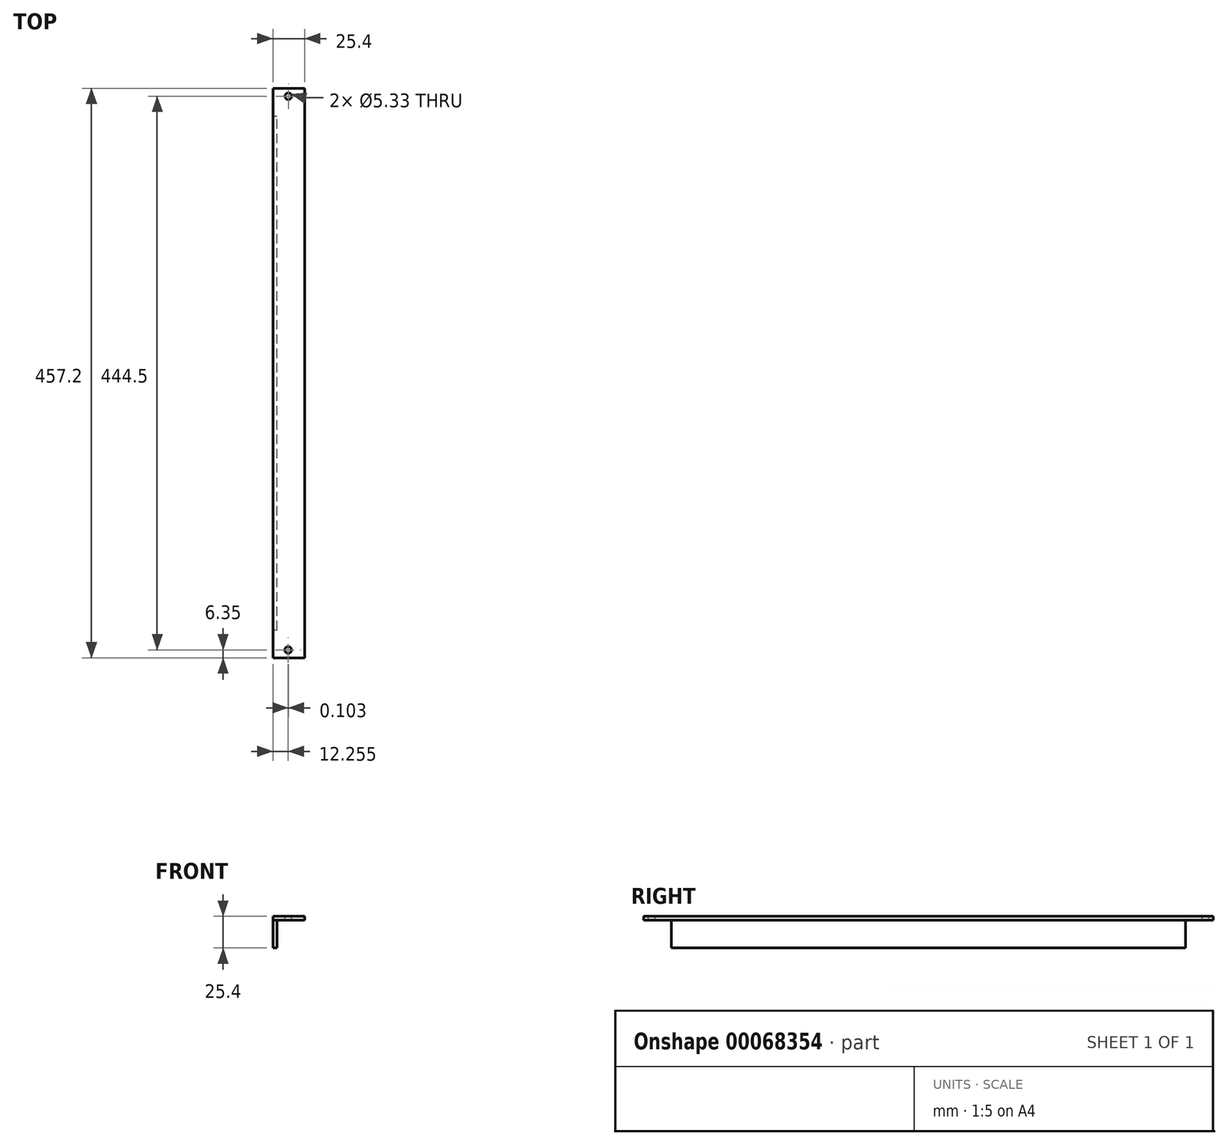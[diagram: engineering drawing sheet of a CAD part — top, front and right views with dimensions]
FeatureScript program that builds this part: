
annotation { "Feature Type Name" : "Feature", "Feature Type Description" : "" }
export const myFeature = defineFeature(function(context is Context, id is Id, definition is map)
    precondition{}
    {
        {
            var Q0;
            Q0=qCreatedBy(makeId("Front.planeOp"),FACE);
            var sketch = newSketch(context, id + "F0", { "sketchPlane" : qUnion([Q0])});
            skLineSegment(sketch, "E0.bottom", {"start": v(-1.59, 12.7) * mm, "end": v(1.59, 12.7) * mm});
            skLineSegment(sketch, "E0.top", {"start": v(-1.59, -12.7) * mm, "end": v(1.59, -12.7) * mm});
            skLineSegment(sketch, "E0.left", {"start": v(-1.59, 12.7) * mm, "end": v(-1.59, -12.7) * mm});
            skLineSegment(sketch, "E0.right", {"start": v(1.59, 9.53) * mm, "end": v(1.59, -12.7) * mm});
            skPoint(sketch, "E0.middle", {"position": v(0, 0) * mm});
            skLineSegment(sketch, "E1.bottom", {"start": v(1.59, 12.7) * mm, "end": v(23.81, 12.7) * mm});
            skLineSegment(sketch, "E1.top", {"start": v(1.59, 9.53) * mm, "end": v(23.81, 9.53) * mm});
            skLineSegment(sketch, "E1.right", {"start": v(23.81, 12.7) * mm, "end": v(23.81, 9.53) * mm});
            skSolve(sketch);
        }
        {
            var Q0;
            Q0=makeQuery(id+"F0.imprint","IMPRINT",FACE,{"disambiguationData":[TD([[makeQuery(id+"F0.imprint","IMPRINT",EDGE,{"derivedFrom":sQuery(id+"F0.wireOp",EDGE,"E0.bottom")}),-1.0]])]});
            extrude(context, id + "F1", {"entities" : qUnion([Q0]), "depth" : 457.2 * mm});
        }
        {
            var Q0;
            Q0=makeQuery(id+"F1.opExtrude","CAP_FACE",FACE,{"disambiguationData":[OSD([sQuery(id+"F0.wireOp",EDGE,"E0.bottom"),sQuery(id+"F0.wireOp",EDGE,"E0.top"),sQuery(id+"F0.wireOp",EDGE,"E0.left"),sQuery(id+"F0.wireOp",EDGE,"E0.right"),sQuery(id+"F0.wireOp",EDGE,"E1.bottom"),sQuery(id+"F0.wireOp",EDGE,"E1.top"),sQuery(id+"F0.wireOp",EDGE,"E1.right")])],"isStart":true});
            var sketch = newSketch(context, id + "F2", { "sketchPlane" : qUnion([Q0])});
            skLineSegment(sketch, "E2.bottom", {"start": v(-1.59, 9.53) * mm, "end": v(1.59, 9.53) * mm});
            skLineSegment(sketch, "E2.top", {"start": v(-1.59, -12.7) * mm, "end": v(1.59, -12.7) * mm});
            skLineSegment(sketch, "E2.left", {"start": v(-1.59, 9.53) * mm, "end": v(-1.59, -12.7) * mm});
            skLineSegment(sketch, "E2.right", {"start": v(1.59, 9.53) * mm, "end": v(1.59, -12.7) * mm});
            skSolve(sketch);
        }
        {
            var Q0;
            Q0=makeQuery(id+"F2.imprint","IMPRINT",FACE,{"disambiguationData":[TD([[makeQuery(id+"F2.imprint","IMPRINT",EDGE,{"derivedFrom":sQuery(id+"F2.wireOp",EDGE,"E2.bottom")}),-1.0]])]});
            extrude(context, id + "F3", {"entities" : qUnion([Q0]), "operationType" : NewBodyOperationType.REMOVE, "oppositeDirection" : true, "depth" : 22.22 * mm});
        }
        {
            var Q0;
            Q0=makeQuery(id+"F1.opExtrude","SWEPT_FACE",FACE,{"disambiguationData":[OSD([sQuery(id+"F0.wireOp",EDGE,"E0.left")])]});
            var sketch = newSketch(context, id + "F4", { "sketchPlane" : qUnion([Q0])});
            skLineSegment(sketch, "E3.bottom", {"start": v(457.2, -12.7) * mm, "end": v(434.98, -12.7) * mm});
            skLineSegment(sketch, "E3.top", {"start": v(457.2, 9.53) * mm, "end": v(434.98, 9.53) * mm});
            skLineSegment(sketch, "E3.left", {"start": v(457.2, -12.7) * mm, "end": v(457.2, 9.53) * mm});
            skLineSegment(sketch, "E3.right", {"start": v(434.98, -12.7) * mm, "end": v(434.98, 9.53) * mm});
            skSolve(sketch);
        }
        {
            var Q0;
            Q0=makeQuery(id+"F4.imprint","IMPRINT",FACE,{"disambiguationData":[TD([[makeQuery(id+"F4.imprint","IMPRINT",EDGE,{"derivedFrom":sQuery(id+"F4.wireOp",EDGE,"E3.bottom")}),-1.0]])]});
            extrude(context, id + "F5", {"entities" : qUnion([Q0]), "operationType" : NewBodyOperationType.REMOVE, "oppositeDirection" : true, "depth" : 3.18 * mm});
        }
        {
            var Q0;
            Q0=makeQuery(id+"F1.opExtrude","SWEPT_FACE",FACE,{"disambiguationData":[OSD([sQuery(id+"F0.wireOp",EDGE,"E0.bottom"),sQuery(id+"F0.wireOp",EDGE,"E1.bottom")])]});
            var sketch = newSketch(context, id + "F6", { "sketchPlane" : qUnion([Q0])});
            skCircle(sketch, "E4", {"center": v(10.66, -450.85) * mm, "radius": 2.67 * mm});
            skCircle(sketch, "E5", {"center": v(10.77, -6.35) * mm, "radius": 2.67 * mm});
            skSolve(sketch);
        }
        {
            var Q0;
            Q0=makeQuery(id+"F6.imprint","IMPRINT",FACE,{"disambiguationData":[TD([[makeQuery(id+"F6.imprint","IMPRINT",EDGE,{"derivedFrom":sQuery(id+"F6.wireOp",EDGE,"E4")}),1.0]])]});
            var Q1;
            Q1=makeQuery(id+"F6.imprint","IMPRINT",FACE,{"disambiguationData":[TD([[makeQuery(id+"F6.imprint","IMPRINT",EDGE,{"derivedFrom":sQuery(id+"F6.wireOp",EDGE,"E5")}),1.0]])]});
            extrude(context, id + "F7", {"entities" : qUnion([Q0, Q1]), "operationType" : NewBodyOperationType.REMOVE, "oppositeDirection" : true, "depth" : 3.17 * mm});
        }
    });
